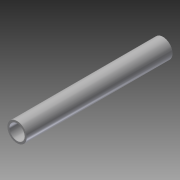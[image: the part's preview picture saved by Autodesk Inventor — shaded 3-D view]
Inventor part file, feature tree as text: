
AUTODESK INVENTOR PART (.ipt)
format: ipt  version: 2013 (Build 170138000, 138)  size: 73,728 bytes
history: native  units: in
note: dims shown in document units (in); Inventor stores cm internally (conversion verified against a paired STEP export)
features: extrude x1, sketch x1
ambient origin geometry x8: Origin, YZ Plane, XZ Plane, XY Plane, X Axis, Y Axis, Z Axis, Center Point
bodies: Solid1 (feature_tree)
feature tree (2):
  extrude  "Extrusion1"  Depth=1.05in
  sketch  "Sketch1"  dims[d0=1.32in d2=1.05in d3=10.0in d4=0.0in]
